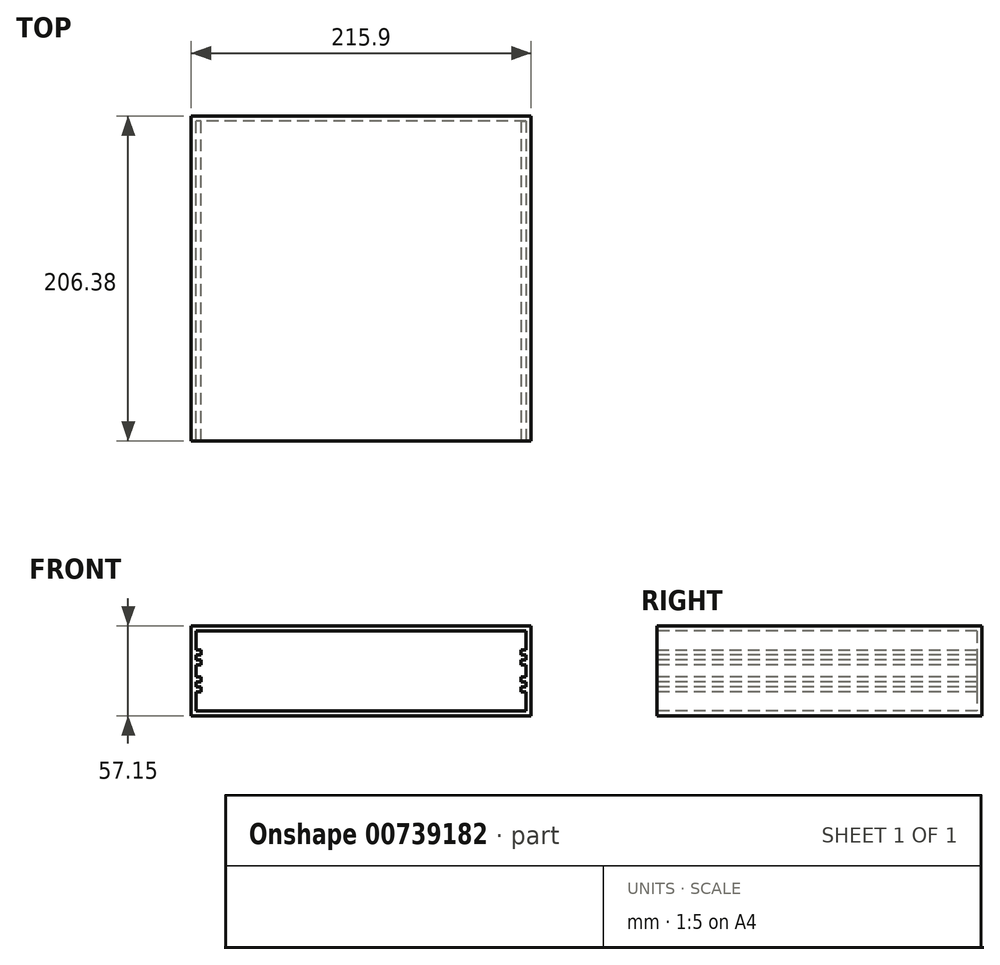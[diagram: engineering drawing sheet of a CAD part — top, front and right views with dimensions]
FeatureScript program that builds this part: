
annotation { "Feature Type Name" : "Feature", "Feature Type Description" : "" }
export const myFeature = defineFeature(function(context is Context, id is Id, definition is map)
    precondition{}
    {
        {
            var Q0;
            Q0=qCreatedBy(makeId("Top.planeOp"),FACE);
            var sketch = newSketch(context, id + "F0", { "sketchPlane" : qUnion([Q0])});
            skLineSegment(sketch, "E0.bottom", {"start": v(107.95, 103.19) * mm, "end": v(-107.95, 103.19) * mm});
            skLineSegment(sketch, "E0.top", {"start": v(107.95, -103.19) * mm, "end": v(-107.95, -103.19) * mm});
            skLineSegment(sketch, "E0.left", {"start": v(107.95, 103.19) * mm, "end": v(107.95, -103.19) * mm});
            skLineSegment(sketch, "E0.right", {"start": v(-107.95, 103.19) * mm, "end": v(-107.95, -103.19) * mm});
            skPoint(sketch, "E0.middle", {"position": v(0, 0) * mm});
            skSolve(sketch);
        }
        {
            var Q0;
            Q0 = qSketchRegion(id + "F0", true);
            extrude(context, id + "F1", {"entities" : qUnion([Q0]), "depth" : 57.15 * mm, "offsetDistance" : 25.4 * mm});
        }
        {
            var Q0;
            Q0=makeQuery(id+"F1.opExtrude","SWEPT_FACE",FACE,{"disambiguationData":[OSD([sQuery(id+"F0.wireOp",EDGE,"E0.top")])]});
            shell(context, id + "F2", {"entities" : qUnion([Q0]), "thickness" : 3.17 * mm});
        }
        {
            var Q0;
            Q0=makeQuery(id+"F2.opShell","OFFSET_FACE",FACE,{"disambiguationData":[OSD([sQuery(id+"F0.wireOp",EDGE,"E0.right")])]});
            var sketch = newSketch(context, id + "F3", { "sketchPlane" : qUnion([Q0])});
            skLineSegment(sketch, "E1", {"start": v(-103.19, 37.04) * mm, "end": v(100.01, 37.04) * mm});
            skLineSegment(sketch, "E2", {"start": v(-103.19, 20.1) * mm, "end": v(100.01, 20.1) * mm});
            skLineSegment(sketch, "E3.bottom", {"start": v(-103.19, 38.63) * mm, "end": v(100.01, 38.63) * mm});
            skLineSegment(sketch, "E3.top", {"start": v(-103.19, 35.45) * mm, "end": v(100.01, 35.45) * mm});
            skLineSegment(sketch, "E3.left", {"start": v(-103.19, 38.63) * mm, "end": v(-103.19, 35.45) * mm});
            skLineSegment(sketch, "E3.right", {"start": v(100.01, 38.63) * mm, "end": v(100.01, 35.45) * mm});
            skLineSegment(sketch, "E4.bottom", {"start": v(-103.19, 21.7) * mm, "end": v(100.01, 21.7) * mm});
            skLineSegment(sketch, "E4.top", {"start": v(-103.19, 18.52) * mm, "end": v(100.01, 18.52) * mm});
            skLineSegment(sketch, "E4.left", {"start": v(-103.19, 21.7) * mm, "end": v(-103.19, 18.52) * mm});
            skLineSegment(sketch, "E4.right", {"start": v(100.01, 21.7) * mm, "end": v(100.01, 18.52) * mm});
            skLineSegment(sketch, "E5", {"start": v(-103.19, 41.8) * mm, "end": v(100.01, 41.8) * mm});
            skLineSegment(sketch, "E6", {"start": v(-103.19, 15.35) * mm, "end": v(100.01, 15.35) * mm});
            skLineSegment(sketch, "E7", {"start": v(-103.19, 32.28) * mm, "end": v(100.01, 32.28) * mm});
            skLineSegment(sketch, "E8", {"start": v(-103.19, 24.87) * mm, "end": v(100.01, 24.87) * mm});
            skSolve(sketch);
        }
        {
            var Q0;
            {var subQ0=sQuery(id+"F3.wireOp",EDGE,"E3.bottom");Q0=makeQuery(id+"F3.imprint","IMPRINT",FACE,{"disambiguationData":[TD([[makeQuery(id+"F3.imprint","IMPRINT",EDGE,{"derivedFrom":subQ0}),1.0]])]});}
            var Q1;
            {var subQ0=sQuery(id+"F3.wireOp",EDGE,"E3.top");Q1=makeQuery(id+"F3.imprint","IMPRINT",FACE,{"disambiguationData":[TD([[makeQuery(id+"F3.imprint","IMPRINT",EDGE,{"derivedFrom":subQ0}),-1.0]])]});}
            var Q2;
            {var subQ0=sQuery(id+"F3.wireOp",EDGE,"E4.bottom");Q2=makeQuery(id+"F3.imprint","IMPRINT",FACE,{"disambiguationData":[TD([[makeQuery(id+"F3.imprint","IMPRINT",EDGE,{"derivedFrom":subQ0}),1.0]])]});}
            var Q3;
            {var subQ0=sQuery(id+"F3.wireOp",EDGE,"E4.top");Q3=makeQuery(id+"F3.imprint","IMPRINT",FACE,{"disambiguationData":[TD([[makeQuery(id+"F3.imprint","IMPRINT",EDGE,{"derivedFrom":subQ0}),-1.0]])]});}
            extrude(context, id + "F4", {"entities" : qUnion([Q0, Q1, Q2, Q3]), "operationType" : NewBodyOperationType.ADD, "depth" : 3.17 * mm, "offsetDistance" : 25.4 * mm});
        }
        {
            var Q0;
            Q0=makeQuery(id+"F2.opShell","OFFSET_FACE",FACE,{"disambiguationData":[OSD([sQuery(id+"F0.wireOp",EDGE,"E0.left")])]});
            var sketch = newSketch(context, id + "F5", { "sketchPlane" : qUnion([Q0])});
            skLineSegment(sketch, "E9", {"start": v(-100.01, 37.04) * mm, "end": v(103.19, 37.04) * mm});
            skLineSegment(sketch, "E10", {"start": v(-100.01, 20.1) * mm, "end": v(103.19, 20.1) * mm});
            skLineSegment(sketch, "E11.bottom", {"start": v(-100.01, 38.63) * mm, "end": v(103.19, 38.63) * mm});
            skLineSegment(sketch, "E11.top", {"start": v(-100.01, 35.45) * mm, "end": v(103.19, 35.45) * mm});
            skLineSegment(sketch, "E11.left", {"start": v(-100.01, 38.63) * mm, "end": v(-100.01, 35.45) * mm});
            skLineSegment(sketch, "E11.right", {"start": v(103.19, 38.63) * mm, "end": v(103.19, 35.45) * mm});
            skLineSegment(sketch, "E12.bottom", {"start": v(-100.01, 21.7) * mm, "end": v(103.19, 21.7) * mm});
            skLineSegment(sketch, "E12.top", {"start": v(-100.01, 18.52) * mm, "end": v(103.19, 18.52) * mm});
            skLineSegment(sketch, "E12.left", {"start": v(-100.01, 21.7) * mm, "end": v(-100.01, 18.52) * mm});
            skLineSegment(sketch, "E12.right", {"start": v(103.19, 21.7) * mm, "end": v(103.19, 18.52) * mm});
            skLineSegment(sketch, "E13", {"start": v(-100.01, 41.8) * mm, "end": v(103.19, 41.8) * mm});
            skLineSegment(sketch, "E14", {"start": v(-100.01, 15.35) * mm, "end": v(103.19, 15.35) * mm});
            skLineSegment(sketch, "E15", {"start": v(-100.01, 32.28) * mm, "end": v(103.19, 32.28) * mm});
            skLineSegment(sketch, "E16", {"start": v(-100.01, 24.87) * mm, "end": v(103.19, 24.87) * mm});
            skSolve(sketch);
        }
        {
            var Q0;
            {var subQ0=sQuery(id+"F5.wireOp",EDGE,"E11.bottom");Q0=makeQuery(id+"F5.imprint","IMPRINT",FACE,{"disambiguationData":[TD([[makeQuery(id+"F5.imprint","IMPRINT",EDGE,{"derivedFrom":subQ0}),1.0]])]});}
            var Q1;
            {var subQ0=sQuery(id+"F5.wireOp",EDGE,"E11.top");Q1=makeQuery(id+"F5.imprint","IMPRINT",FACE,{"disambiguationData":[TD([[makeQuery(id+"F5.imprint","IMPRINT",EDGE,{"derivedFrom":subQ0}),-1.0]])]});}
            var Q2;
            {var subQ0=sQuery(id+"F5.wireOp",EDGE,"E12.bottom");Q2=makeQuery(id+"F5.imprint","IMPRINT",FACE,{"disambiguationData":[TD([[makeQuery(id+"F5.imprint","IMPRINT",EDGE,{"derivedFrom":subQ0}),1.0]])]});}
            var Q3;
            {var subQ0=sQuery(id+"F5.wireOp",EDGE,"E12.top");Q3=makeQuery(id+"F5.imprint","IMPRINT",FACE,{"disambiguationData":[TD([[makeQuery(id+"F5.imprint","IMPRINT",EDGE,{"derivedFrom":subQ0}),-1.0]])]});}
            extrude(context, id + "F6", {"entities" : qUnion([Q0, Q1, Q2, Q3]), "operationType" : NewBodyOperationType.ADD, "depth" : 3.17 * mm, "offsetDistance" : 25.4 * mm});
        }
    });
